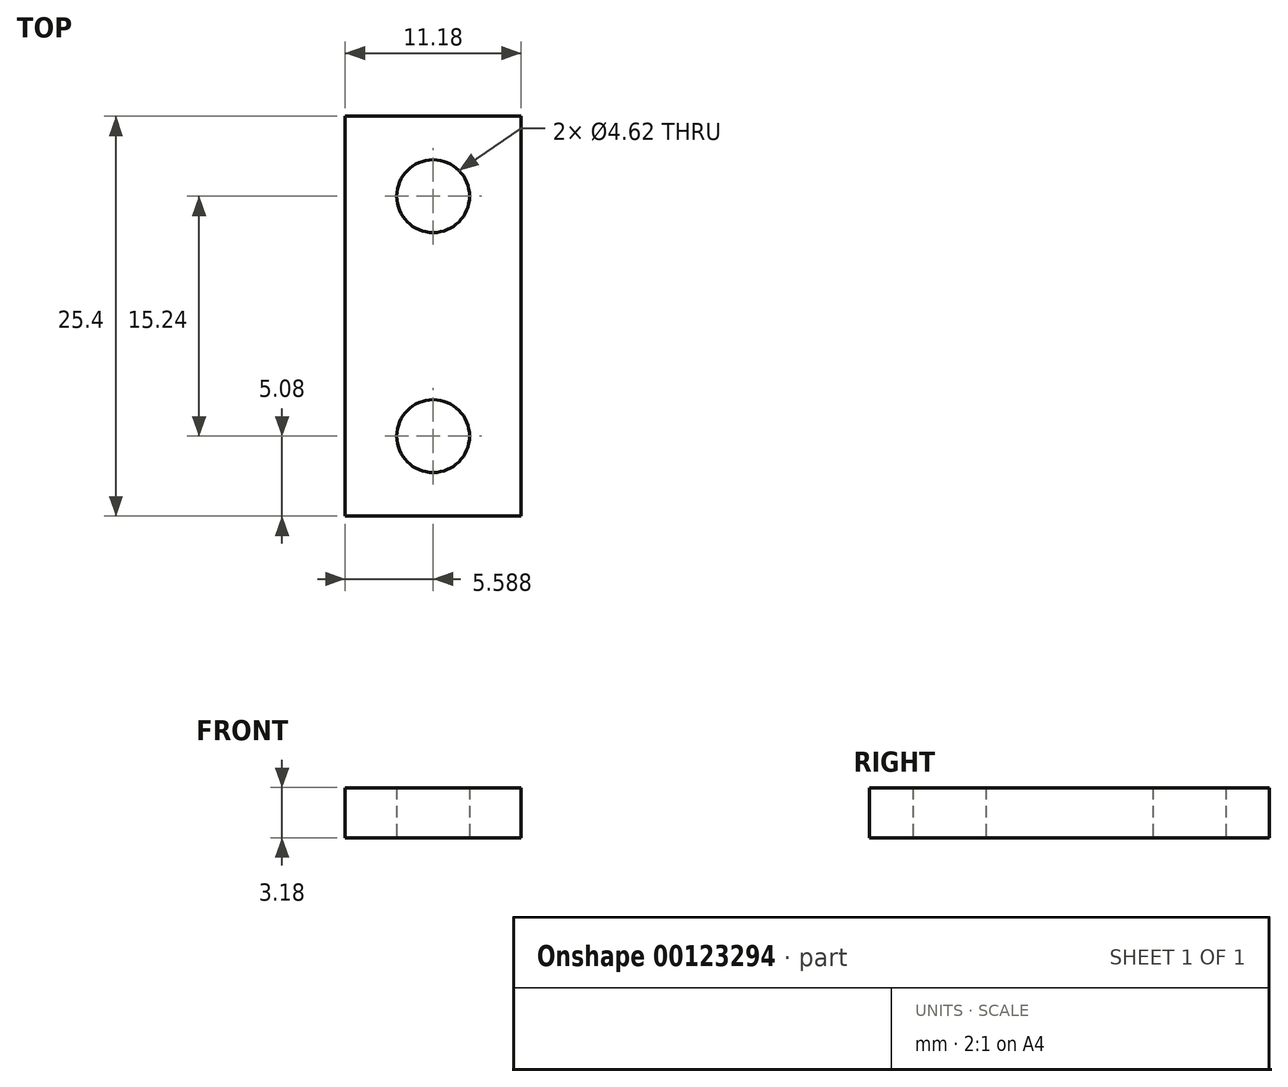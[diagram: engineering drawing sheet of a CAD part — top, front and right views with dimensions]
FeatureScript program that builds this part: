
annotation { "Feature Type Name" : "Feature", "Feature Type Description" : "" }
export const myFeature = defineFeature(function(context is Context, id is Id, definition is map)
    precondition{}
    {
        {
            var Q0;
            Q0=qCreatedBy(makeId("Top.planeOp"),FACE);
            var sketch = newSketch(context, id + "F0", { "sketchPlane" : qUnion([Q0])});
            skLineSegment(sketch, "E0.bottom", {"start": v(0, 0) * mm, "end": v(11.18, 0) * mm});
            skLineSegment(sketch, "E0.top", {"start": v(0, 25.4) * mm, "end": v(11.18, 25.4) * mm});
            skLineSegment(sketch, "E0.left", {"start": v(0, 0) * mm, "end": v(0, 25.4) * mm});
            skLineSegment(sketch, "E0.right", {"start": v(11.18, 0) * mm, "end": v(11.18, 25.4) * mm});
            skPoint(sketch, "E1", {"position": v(5.59, 25.4) * mm});
            skPoint(sketch, "E2", {"position": v(5.59, 0) * mm});
            skPoint(sketch, "E3", {"position": v(11.18, 5.08) * mm});
            skPoint(sketch, "E4", {"position": v(11.18, 20.32) * mm});
            skCircle(sketch, "E5", {"center": v(5.59, 20.32) * mm, "radius": 2.31 * mm});
            skCircle(sketch, "E6", {"center": v(5.59, 5.08) * mm, "radius": 2.31 * mm});
            skSolve(sketch);
        }
        {
            var Q0;
            Q0=makeQuery(id+"F0.imprint","IMPRINT",FACE,{"disambiguationData":[TD([[makeQuery(id+"F0.imprint","IMPRINT",EDGE,{"derivedFrom":sQuery(id+"F0.wireOp",EDGE,"E0.bottom")}),1.0]])]});
            extrude(context, id + "F1", {"entities" : qUnion([Q0]), "depth" : 3.17 * mm});
        }
    });
